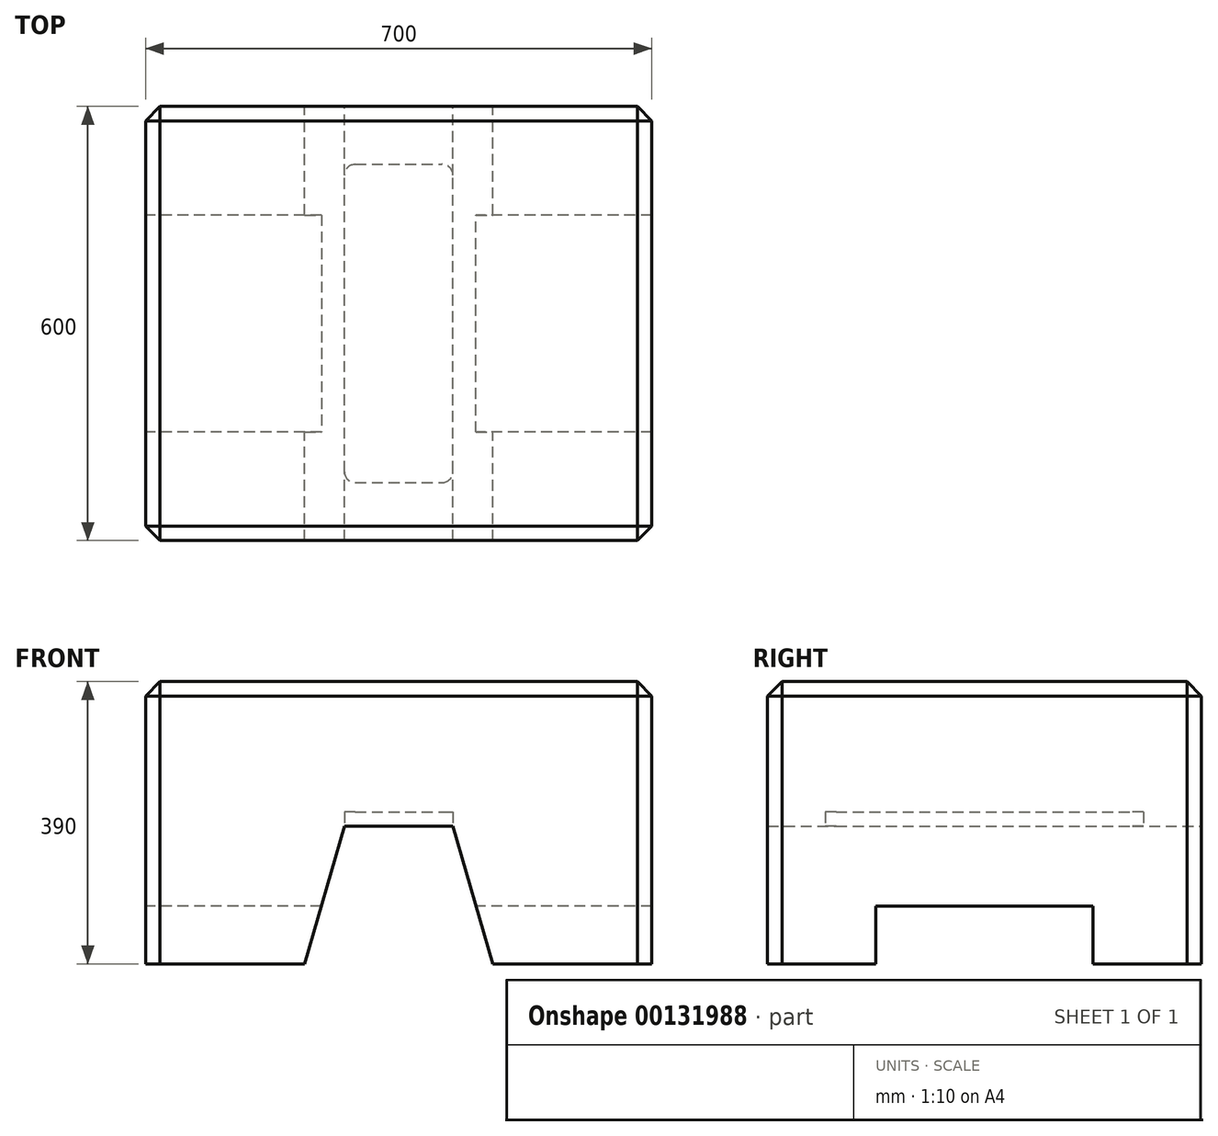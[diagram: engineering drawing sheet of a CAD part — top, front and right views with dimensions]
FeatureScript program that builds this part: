
annotation { "Feature Type Name" : "Feature", "Feature Type Description" : "" }
export const myFeature = defineFeature(function(context is Context, id is Id, definition is map)
    precondition{}
    {
        {
            var Q0;
            Q0=qCreatedBy(makeId("Front.planeOp"),FACE);
            var sketch = newSketch(context, id + "F0", { "sketchPlane" : qUnion([Q0])});
            skLineSegment(sketch, "E0.bottom", {"start": v(0, 0) * mm, "end": v(-220, 0) * mm});
            skLineSegment(sketch, "E0.top", {"start": v(0, 390) * mm, "end": v(-700, 390) * mm});
            skLineSegment(sketch, "E0.left", {"start": v(0, 0) * mm, "end": v(0, 390) * mm});
            skLineSegment(sketch, "E0.right", {"start": v(-700, 0) * mm, "end": v(-700, 390) * mm});
            skLineSegment(sketch, "E1", {"start": v(-480, 0) * mm, "end": v(-425, 190) * mm});
            skLineSegment(sketch, "E2", {"start": v(-425, 190) * mm, "end": v(-275, 190) * mm});
            skLineSegment(sketch, "E3", {"start": v(-275, 190) * mm, "end": v(-220, 0) * mm});
            skLineSegment(sketch, "E4.trimOffspring", {"start": v(-480, 0) * mm, "end": v(-700, 0) * mm});
            skSolve(sketch);
        }
        {
            var Q0;
            Q0=makeQuery(id+"F0.imprint","IMPRINT",FACE,{"disambiguationData":[TD([[makeQuery(id+"F0.imprint","IMPRINT",EDGE,{"derivedFrom":sQuery(id+"F0.wireOp",EDGE,"E0.bottom")}),-1.0]])]});
            extrude(context, id + "F1", {"entities" : qUnion([Q0]), "depth" : 600 * mm});
        }
        {
            var Q0;
            Q0=makeQuery(id+"F1.opExtrude","SWEPT_FACE",FACE,{"disambiguationData":[OSD([sQuery(id+"F0.wireOp",EDGE,"E0.bottom")])]});
            var sketch = newSketch(context, id + "F2", { "sketchPlane" : qUnion([Q0])});
            skLineSegment(sketch, "E5.bottom", {"start": v(30, 150) * mm, "end": v(-730, 150) * mm});
            skLineSegment(sketch, "E5.top", {"start": v(30, 450) * mm, "end": v(-730, 450) * mm});
            skLineSegment(sketch, "E5.left", {"start": v(30, 150) * mm, "end": v(30, 450) * mm});
            skLineSegment(sketch, "E5.right", {"start": v(-730, 150) * mm, "end": v(-730, 450) * mm});
            skSolve(sketch);
        }
        {
            var Q0;
            Q0=qSketchRegion(id+"F2",true);
            extrude(context, id + "F3", {"entities" : qUnion([Q0]), "operationType" : NewBodyOperationType.REMOVE, "oppositeDirection" : true, "depth" : 80 * mm});
        }
        {
            var Q0;
            Q0=makeQuery(id+"F1.opExtrude","SWEPT_FACE",FACE,{"disambiguationData":[OSD([sQuery(id+"F0.wireOp",EDGE,"E2")])]});
            var sketch = newSketch(context, id + "F4", { "sketchPlane" : qUnion([Q0])});
            skLineSegment(sketch, "E6.bottom", {"start": v(-425, 80) * mm, "end": v(-275, 80) * mm});
            skLineSegment(sketch, "E6.top", {"start": v(-425, 520) * mm, "end": v(-275, 520) * mm});
            skLineSegment(sketch, "E6.left", {"start": v(-425, 80) * mm, "end": v(-425, 520) * mm});
            skLineSegment(sketch, "E6.right", {"start": v(-275, 80) * mm, "end": v(-275, 520) * mm});
            skSolve(sketch);
        }
        {
            var Q0;
            Q0=qSketchRegion(id+"F4",true);
            extrude(context, id + "F5", {"entities" : qUnion([Q0]), "operationType" : NewBodyOperationType.REMOVE, "oppositeDirection" : true, "depth" : 20 * mm});
        }
        {
            var Q0;
            Q0=makeQuery(id+"F1.opExtrude","CAP_EDGE",EDGE,{"disambiguationData":[OSD([sQuery(id+"F0.wireOp",EDGE,"E0.right")])],"isStart":true});
            var Q1;
            Q1=makeQuery(id+"F1.opExtrude","SWEPT_EDGE",EDGE,{"disambiguationData":[OSD([sQuery(id+"F0.wireOp",EDGE,"E0.top"),sQuery(id+"F0.wireOp",EDGE,"E0.right")])]});
            var Q2;
            Q2=makeQuery(id+"F1.opExtrude","CAP_EDGE",EDGE,{"disambiguationData":[OSD([sQuery(id+"F0.wireOp",EDGE,"E0.top")])],"isStart":true});
            var Q3;
            Q3=makeQuery(id+"F1.opExtrude","SWEPT_EDGE",EDGE,{"disambiguationData":[OSD([sQuery(id+"F0.wireOp",EDGE,"E0.top"),sQuery(id+"F0.wireOp",EDGE,"E0.left")])]});
            var Q4;
            Q4=makeQuery(id+"F1.opExtrude","CAP_EDGE",EDGE,{"disambiguationData":[OSD([sQuery(id+"F0.wireOp",EDGE,"E0.top")])],"isStart":false});
            var Q5;
            Q5=makeQuery(id+"F1.opExtrude","CAP_EDGE",EDGE,{"disambiguationData":[OSD([sQuery(id+"F0.wireOp",EDGE,"E0.right")])],"isStart":false});
            var Q6;
            Q6=makeQuery(id+"F1.opExtrude","CAP_EDGE",EDGE,{"disambiguationData":[OSD([sQuery(id+"F0.wireOp",EDGE,"E0.left")])],"isStart":false});
            var Q7;
            Q7=makeQuery(id+"F1.opExtrude","CAP_EDGE",EDGE,{"disambiguationData":[OSD([sQuery(id+"F0.wireOp",EDGE,"E0.left")])],"isStart":true});
            chamfer(context, id + "F6", {"entities" : qUnion([Q0, Q1, Q2, Q3, Q4, Q5, Q6, Q7]), "width" : 20 * mm, "tangentPropagation" : true});
        }
        {
            var Q0;
            Q0=makeQuery(id+"F5.boolean.opBoolean","COPY",EDGE,{"derivedFrom":makeQuery(id+"F5.opExtrude","SWEPT_EDGE",EDGE,{"disambiguationData":[OSD([sQuery(id+"F0.wireOp",EDGE,"E2"),sQuery(id+"F0.wireOp",EDGE,"E3"),sQuery(id+"F4.wireOp",EDGE,"E6.top"),sQuery(id+"F4.wireOp",EDGE,"E6.right")])]})});
            var Q1;
            Q1=makeQuery(id+"F5.boolean.opBoolean","COPY",EDGE,{"derivedFrom":makeQuery(id+"F5.opExtrude","SWEPT_EDGE",EDGE,{"disambiguationData":[OSD([sQuery(id+"F0.wireOp",EDGE,"E1"),sQuery(id+"F0.wireOp",EDGE,"E2"),sQuery(id+"F4.wireOp",EDGE,"E6.top"),sQuery(id+"F4.wireOp",EDGE,"E6.left")])]})});
            var Q2;
            Q2=makeQuery(id+"F5.boolean.opBoolean","COPY",EDGE,{"derivedFrom":makeQuery(id+"F5.opExtrude","SWEPT_EDGE",EDGE,{"disambiguationData":[OSD([sQuery(id+"F0.wireOp",EDGE,"E1"),sQuery(id+"F0.wireOp",EDGE,"E2"),sQuery(id+"F4.wireOp",EDGE,"E6.bottom"),sQuery(id+"F4.wireOp",EDGE,"E6.left")])]})});
            var Q3;
            Q3=makeQuery(id+"F5.boolean.opBoolean","COPY",EDGE,{"derivedFrom":makeQuery(id+"F5.opExtrude","SWEPT_EDGE",EDGE,{"disambiguationData":[OSD([sQuery(id+"F0.wireOp",EDGE,"E2"),sQuery(id+"F0.wireOp",EDGE,"E3"),sQuery(id+"F4.wireOp",EDGE,"E6.bottom"),sQuery(id+"F4.wireOp",EDGE,"E6.right")])]})});
            fillet(context, id + "F7", {"entities" : qUnion([Q0, Q1, Q2, Q3]), "radius" : 15 * mm, "tangentPropagation" : true, "allowEdgeOverflow" : false});
        }
    });
